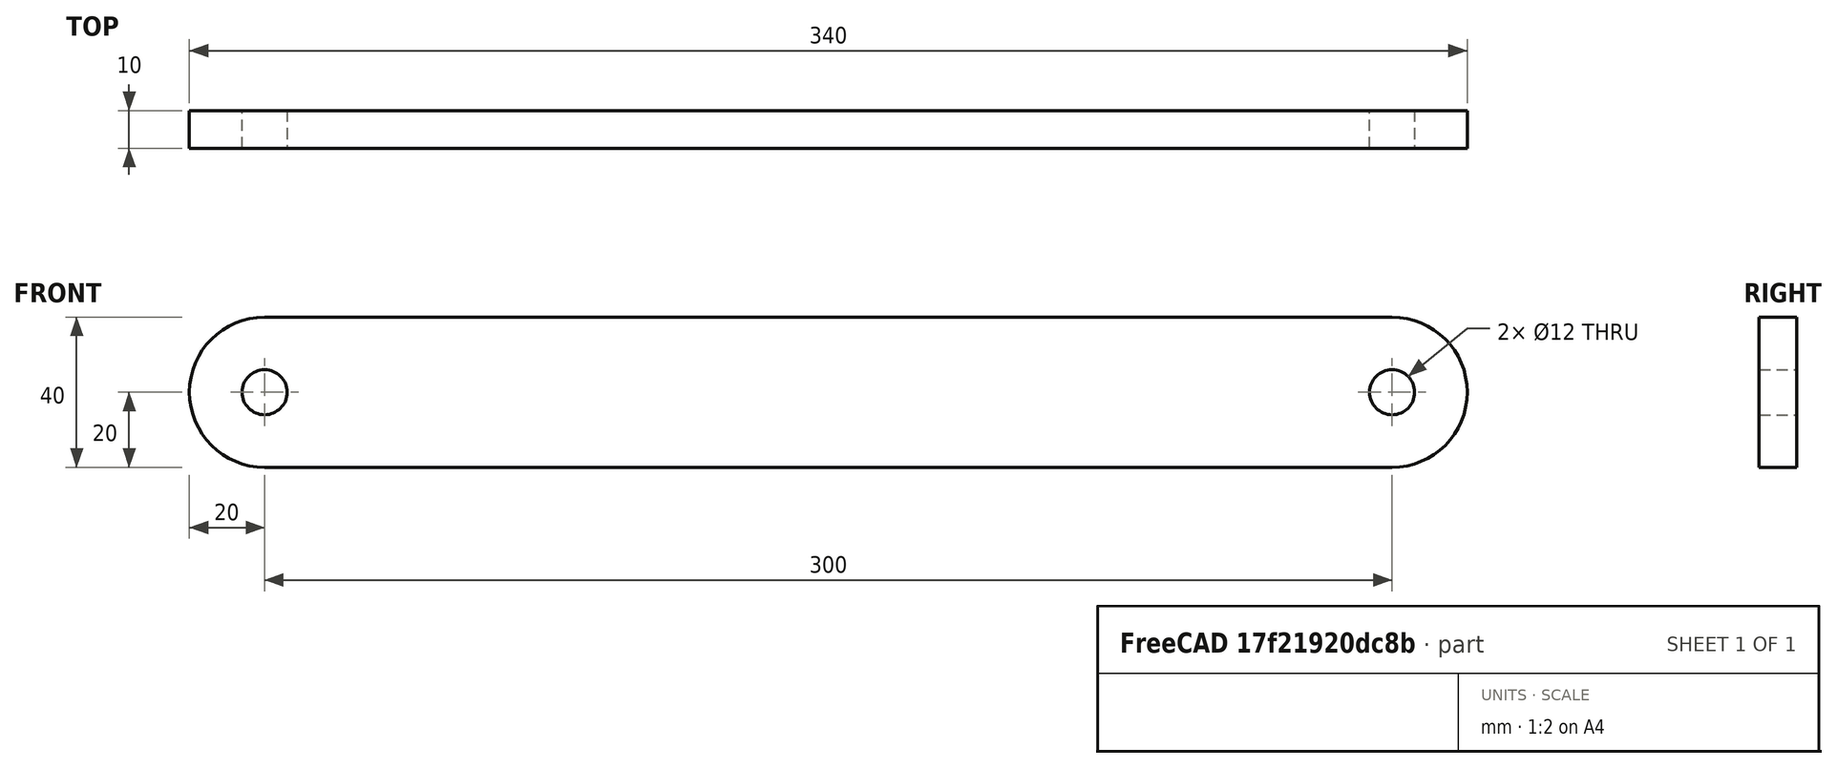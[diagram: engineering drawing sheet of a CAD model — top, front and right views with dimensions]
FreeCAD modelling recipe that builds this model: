
FCSTD DOCUMENT  (FreeCAD 0.19R24212 (Git))
Label: Bielle2
License: Creative Commons Attribution
LicenseURL: http://creativecommons.org/licenses/by/4.0/
objects: Sketcher::SketchObject×1, PartDesign::Pad×1, PartDesign::CoordinateSystem×1, PartDesign::Body×1
note: 5 computed .brp shape members not serialized (recipe doc carries the construction recipe); baked Part::Feature solids carry a one-line shape summary decoded from their .brp

FEATURE [Sketcher::SketchObject] Sketch
  FullyConstrained = true
  MapMode = 5
  Placement = pos=(0,0,0) rot=(1,0,0;1.5708rad)
  Support = -> [XZ_Plane]
  sketch-geometry (6):
    g0: Circle CenterX=0 CenterY=0 CenterZ=0 NormalX=0 NormalY=0 NormalZ=1 AngleXU=0 Radius=6
    g1: Circle CenterX=300 CenterY=0 CenterZ=0 NormalX=0 NormalY=0 NormalZ=1 AngleXU=0 Radius=6
    g2: ArcOfCircle CenterX=0 CenterY=0 CenterZ=0 NormalX=0 NormalY=0 NormalZ=1 AngleXU=0 Radius=20 StartAngle=1.5708 EndAngle=4.71239
    g3: ArcOfCircle CenterX=300 CenterY=0 CenterZ=0 NormalX=0 NormalY=0 NormalZ=1 AngleXU=0 Radius=20 StartAngle=4.71239 EndAngle=7.85398
    g4: LineSegment StartX=0 StartY=-20 StartZ=0 EndX=300 EndY=-20 EndZ=0
    g5: LineSegment StartX=-3.2e-15 StartY=20 StartZ=0 EndX=300 EndY=20 EndZ=0
  constraints (13):
    c: Coincident(g0,g-1)
    c: PointOnObject(g1,g-1)
    c: Tangent(g2,g5) = 1.5708
    c: Tangent(g2,g4) = -1.5708
    c: Tangent(g4,g3) = -1.5708
    c: Tangent(g5,g3) = 1.5708
    c: Horizontal(g4)
    c: Coincident(g2,g0)
    c: Coincident(g1,g3)
    c: Equal(g0,g1)
    c: Radius(g2) = 20
    c: Radius(g0) = 6
    c: DistanceX(g0,g1) = 300
FEATURE [PartDesign::Pad] Pad
  Direction = (1,1,1)
  Length = 10
  Length2 = 100
  Placement = pos=(0,0,0) rot=(1,0,0;1.5708rad)
  Profile = -> Sketch
  Refine = true
  Type = 0
FEATURE [PartDesign::CoordinateSystem] Local_CS
  AttacherType = Attacher::AttachEngine3D
  MapMode = 11
  Placement = pos=(0,0,0) rot=(0.57735,-0.57735,0.57735;2.0944rad)
  Support = -> [Sketch]
FEATURE [PartDesign::Body] Body
  Group = -> [Sketch,Pad,Local_CS]
  Origin = -> Origin
  Tip = -> Pad
